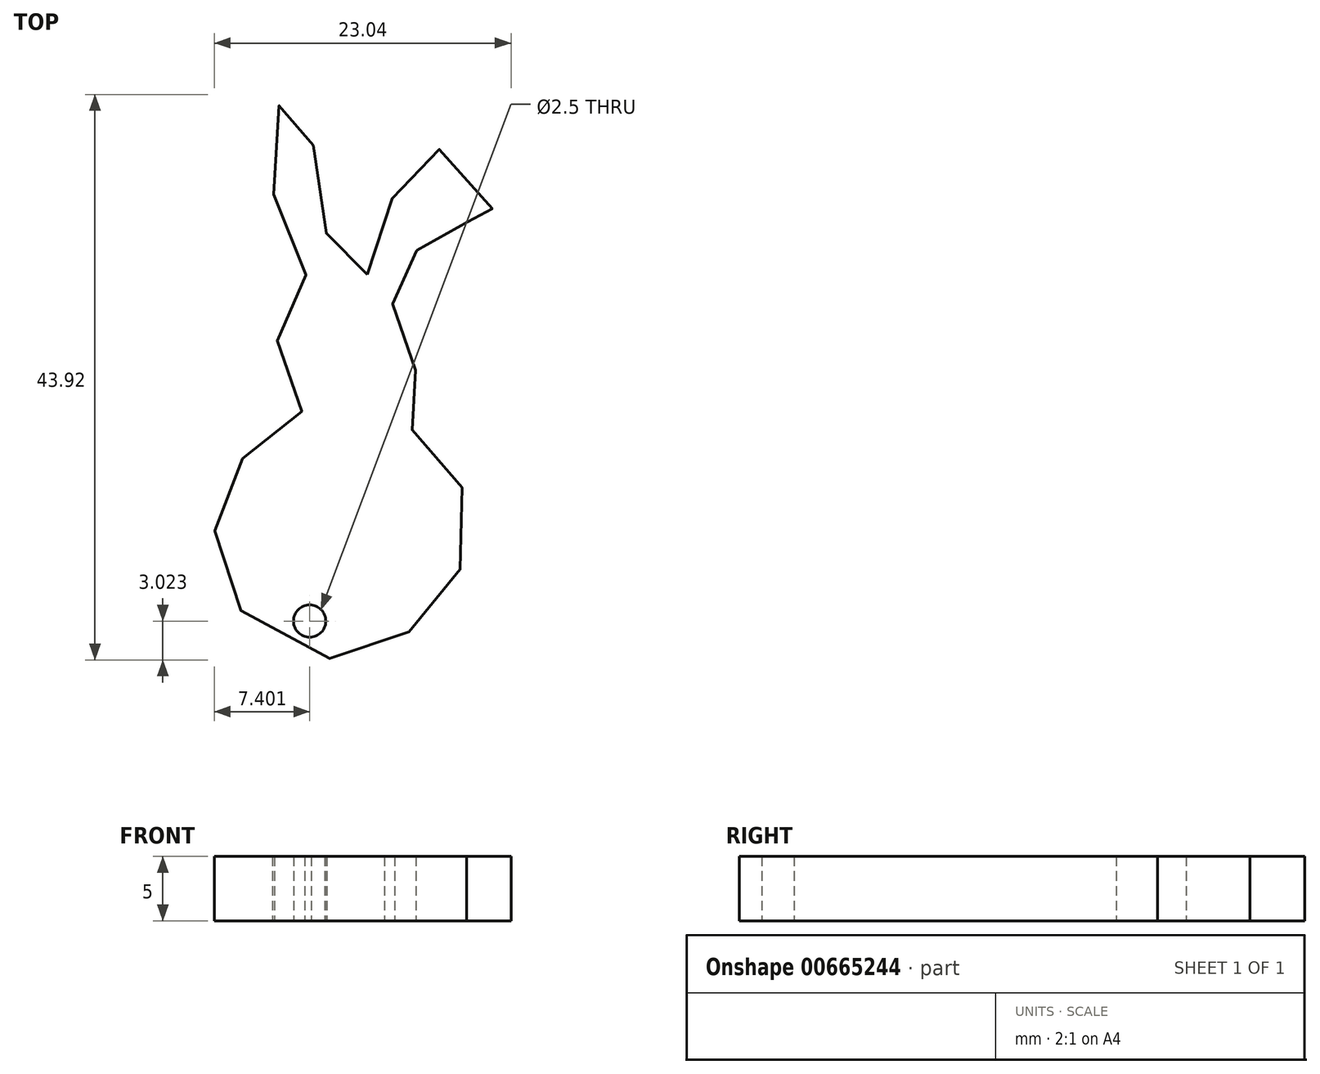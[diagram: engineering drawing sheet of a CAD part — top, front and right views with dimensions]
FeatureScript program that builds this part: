
annotation { "Feature Type Name" : "Feature", "Feature Type Description" : "" }
export const myFeature = defineFeature(function(context is Context, id is Id, definition is map)
    precondition{}
    {
        {
            var Q0;
            Q0=qCreatedBy(makeId("Top.planeOp"),FACE);
            var sketch = newSketch(context, id + "F0", { "sketchPlane" : qUnion([Q0])});
            skFitSpline(sketch, "E0", {"points": [v(-39.16, 35.06) * mm, v(-38.15, 39.1) * mm, v(-37.14, 41.07) * mm, v(-35.5, 43.09) * mm, v(-33.82, 44.77) * mm, v(-31.7, 43.6) * mm, v(-29.67, 40.5) * mm, v(-28.04, 37.64) * mm, v(-31.75, 39.38) * mm, v(-32.98, 39.77) * mm, v(-34.78, 37.53) * mm, v(-37.14, 35.06) * mm, v(-37.75, 33.49) * mm, v(-36.3, 32.03) * mm, v(-35.56, 30.23) * mm, v(-35.73, 26.41) * mm, v(-37.02, 24.56) * mm, v(-35, 22.54) * mm, v(-32.87, 20.85) * mm, v(-31.58, 17.7) * mm, v(-31.52, 14.73) * mm, v(-32.42, 10.75) * mm, v(-34.55, 8.33) * mm, v(-37.36, 6.31) * mm, v(-40.34, 5.13) * mm, v(-46.96, 6.93) * mm, v(-49.26, 9.4) * mm, v(-50.84, 12.54) * mm, v(-50.72, 16.7) * mm, v(-49.66, 19.45) * mm, v(-48.09, 21.7) * mm, v(-45.78, 23.55) * mm, v(-43.99, 24.9) * mm, v(-46.18, 27.87) * mm, v(-45.17, 31.52) * mm, v(-43.48, 33.88) * mm, v(-44.77, 36.24) * mm, v(-46.23, 40.06) * mm, v(-46.46, 43.99) * mm, v(-46, 48.08) * mm, v(-45.73, 49.04) * mm, v(-44.04, 46.8) * mm, v(-42.7, 42.53) * mm, v(-42.3, 38.7) * mm, v(-41.97, 34.83) * mm, v(-39.16, 35.06) * mm]});
            skCircle(sketch, "E1", {"center": v(-43.62, 8.14) * mm, "radius": 1.25 * mm});
            skSolve(sketch);
        }
        {
            var Q0;
            Q0=makeQuery(id+"F0.imprint","IMPRINT",FACE,{"disambiguationData":[TD([[makeQuery(id+"F0.imprint","IMPRINT",EDGE,{"derivedFrom":sQuery(id+"F0.wireOp",EDGE,"E0")}),-1.0]])]});
            extrude(context, id + "F1", {"entities" : qUnion([Q0]), "depth" : 5 * mm, "offsetDistance" : 25 * mm});
        }
    });
